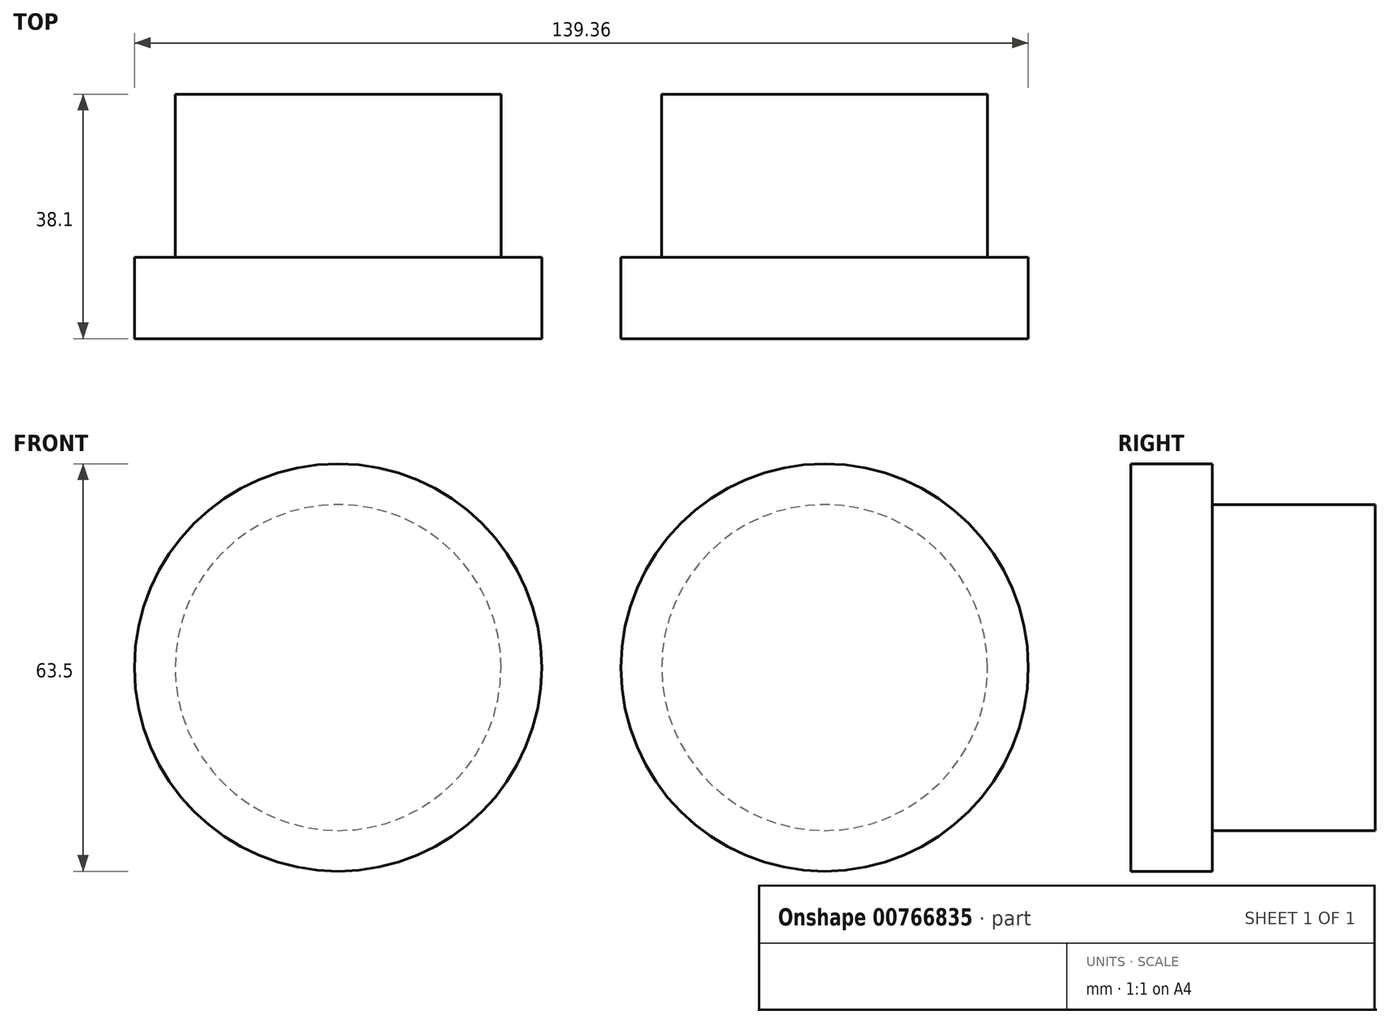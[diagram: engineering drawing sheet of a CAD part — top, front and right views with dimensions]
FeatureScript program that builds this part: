
annotation { "Feature Type Name" : "Feature", "Feature Type Description" : "" }
export const myFeature = defineFeature(function(context is Context, id is Id, definition is map)
    precondition{}
    {
        {
            var Q0;
            Q0=qCreatedBy(makeId("Front.planeOp"),FACE);
            var sketch = newSketch(context, id + "F0", { "sketchPlane" : qUnion([Q0])});
            skPoint(sketch, "E0.middle", {"position": v(0, 0) * mm});
            skCircle(sketch, "E1", {"center": v(-37.02, 0) * mm, "radius": 25.4 * mm});
            skCircle(sketch, "E2", {"center": v(38.84, 0) * mm, "radius": 25.4 * mm});
            skSolve(sketch);
        }
        {
            var Q0;
            Q0 = qSketchRegion(id + "F0", true);
            extrude(context, id + "F1", {"entities" : qUnion([Q0]), "depth" : 25.4 * mm, "offsetDistance" : 25.4 * mm});
        }
        {
            var Q0;
            Q0=makeQuery(id+"F1.opExtrude","CAP_FACE",FACE,{"disambiguationData":[OSD([sQuery(id+"F0.wireOp",EDGE,"E1")])],"isStart":false});
            var sketch = newSketch(context, id + "F2", { "sketchPlane" : qUnion([Q0])});
            skCircle(sketch, "E3", {"center": v(-37.02, 0) * mm, "radius": 31.75 * mm});
            skSolve(sketch);
        }
        {
            var Q0;
            Q0 = qSketchRegion(id + "F2", true);
            extrude(context, id + "F3", {"entities" : qUnion([Q0]), "operationType" : NewBodyOperationType.ADD, "depth" : 12.7 * mm, "offsetDistance" : 25.4 * mm});
        }
        {
            var Q0;
            Q0=makeQuery(id+"F1.opExtrude","CAP_FACE",FACE,{"disambiguationData":[OSD([sQuery(id+"F0.wireOp",EDGE,"E2")])],"isStart":false});
            var sketch = newSketch(context, id + "F4", { "sketchPlane" : qUnion([Q0])});
            skCircle(sketch, "E4", {"center": v(38.84, 0) * mm, "radius": 31.75 * mm});
            skSolve(sketch);
        }
        {
            var Q0;
            Q0 = qSketchRegion(id + "F4", true);
            extrude(context, id + "F5", {"entities" : qUnion([Q0]), "operationType" : NewBodyOperationType.ADD, "depth" : 12.7 * mm, "offsetDistance" : 25.4 * mm});
        }
    });
